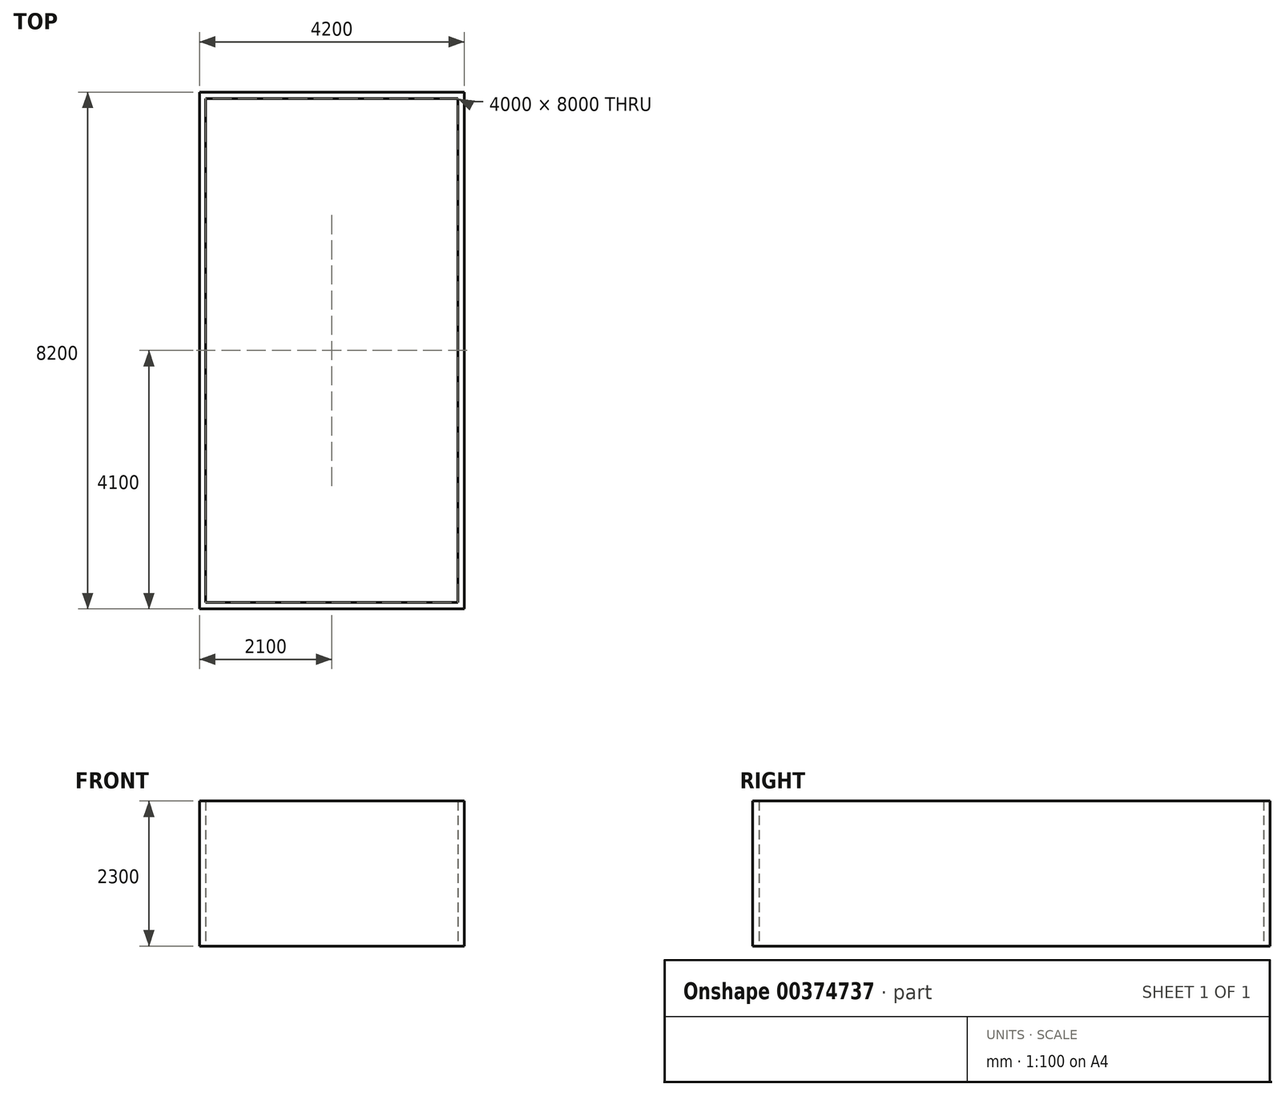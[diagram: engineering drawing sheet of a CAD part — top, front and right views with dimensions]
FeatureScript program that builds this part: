
annotation { "Feature Type Name" : "Feature", "Feature Type Description" : "" }
export const myFeature = defineFeature(function(context is Context, id is Id, definition is map)
    precondition{}
    {
        {
            var Q0;
            Q0=qCreatedBy(makeId("Top.planeOp"),FACE);
            var sketch = newSketch(context, id + "F0", { "sketchPlane" : qUnion([Q0])});
            skLineSegment(sketch, "E0.bottom", {"start": v(0, 0) * mm, "end": v(4200, 0) * mm});
            skLineSegment(sketch, "E0.top", {"start": v(0, 8200) * mm, "end": v(4200, 8200) * mm});
            skLineSegment(sketch, "E0.left", {"start": v(0, 0) * mm, "end": v(0, 8200) * mm});
            skLineSegment(sketch, "E0.right", {"start": v(4200, 0) * mm, "end": v(4200, 8200) * mm});
            skLineSegment(sketch, "E1.bottom", {"start": v(100, 8100) * mm, "end": v(4100, 8100) * mm});
            skLineSegment(sketch, "E1.top", {"start": v(100, 100) * mm, "end": v(4100, 100) * mm});
            skLineSegment(sketch, "E1.left", {"start": v(100, 8100) * mm, "end": v(100, 100) * mm});
            skLineSegment(sketch, "E1.right", {"start": v(4100, 8100) * mm, "end": v(4100, 100) * mm});
            skSolve(sketch);
        }
        {
            var Q0;
            Q0=makeQuery(id+"F0.imprint","IMPRINT",FACE,{"disambiguationData":[TD([[makeQuery(id+"F0.imprint","IMPRINT",EDGE,{"derivedFrom":sQuery(id+"F0.wireOp",EDGE,"E0.bottom")}),1.0]])]});
            extrude(context, id + "F1", {"entities" : qUnion([Q0]), "depth" : 2300 * mm});
        }
    });
